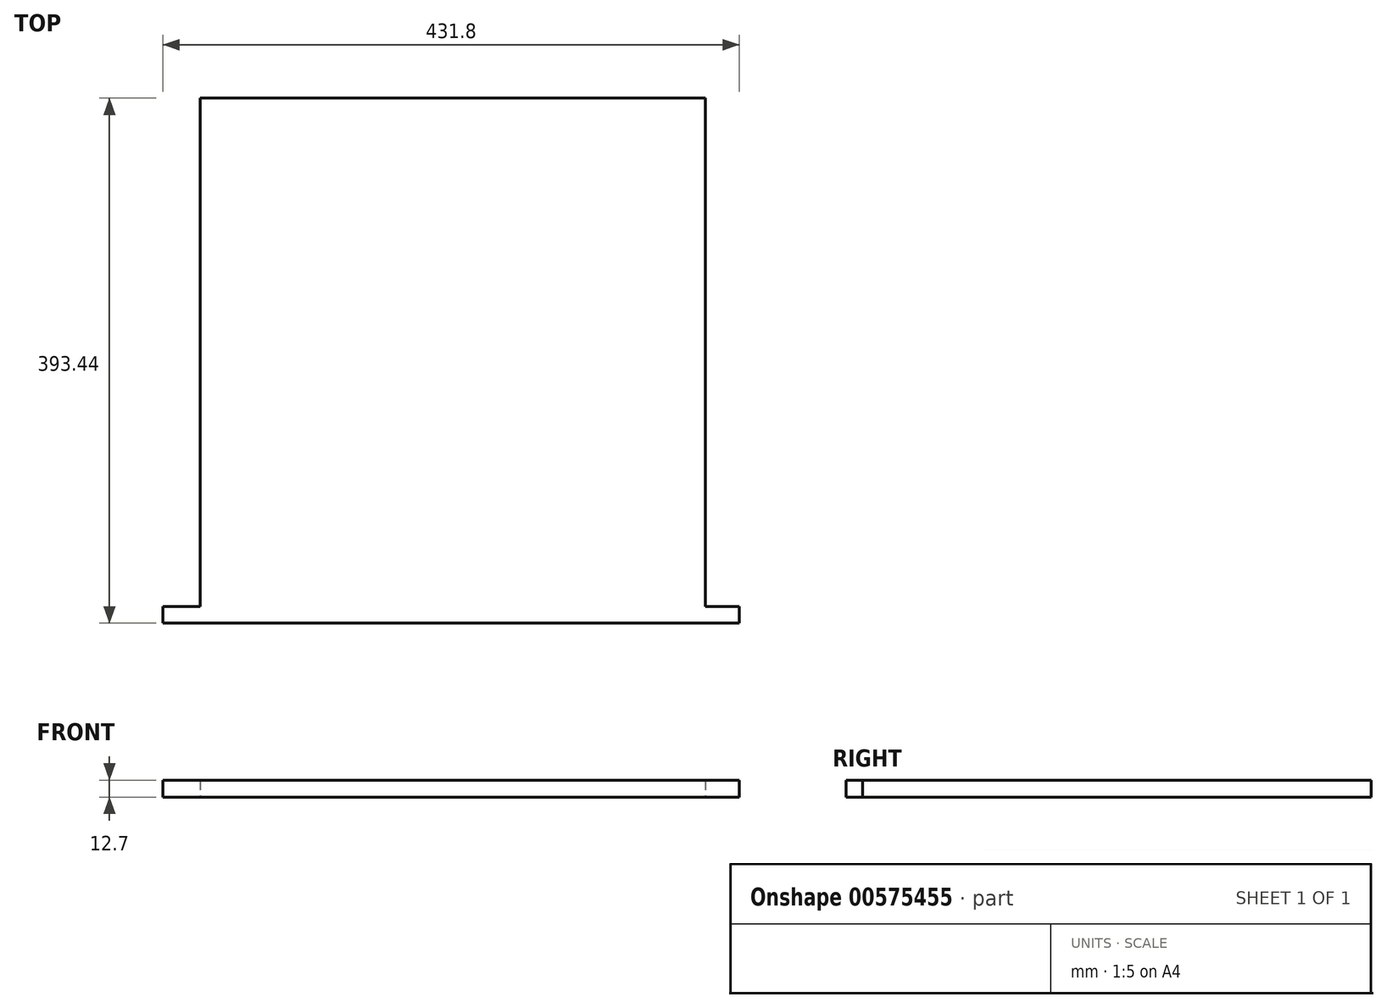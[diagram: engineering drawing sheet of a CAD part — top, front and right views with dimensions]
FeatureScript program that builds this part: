
annotation { "Feature Type Name" : "Feature", "Feature Type Description" : "" }
export const myFeature = defineFeature(function(context is Context, id is Id, definition is map)
    precondition{}
    {
        {
            var Q0;
            Q0=qCreatedBy(makeId("Top.planeOp"),FACE);
            var sketch = newSketch(context, id + "F0", { "sketchPlane" : qUnion([Q0])});
            skLineSegment(sketch, "E0", {"start": v(-215.51, -21.57) * mm, "end": v(-215.51, -34.01) * mm});
            skLineSegment(sketch, "E1", {"start": v(-215.51, -34.01) * mm, "end": v(216.29, -34.01) * mm});
            skLineSegment(sketch, "E2", {"start": v(216.29, -34.01) * mm, "end": v(216.29, -21.57) * mm});
            skLineSegment(sketch, "E3", {"start": v(-215.51, -21.57) * mm, "end": v(-187.57, -21.57) * mm});
            skLineSegment(sketch, "E4", {"start": v(-187.57, -21.57) * mm, "end": v(-187.57, 359.43) * mm});
            skLineSegment(sketch, "E5", {"start": v(216.29, -21.57) * mm, "end": v(190.89, -21.57) * mm});
            skLineSegment(sketch, "E6", {"start": v(190.89, -21.57) * mm, "end": v(190.89, 359.43) * mm});
            skLineSegment(sketch, "E7", {"start": v(190.89, 359.43) * mm, "end": v(-187.57, 359.43) * mm});
            skSolve(sketch);
        }
        {
            var Q0;
            Q0 = qSketchRegion(id + "F0", true);
            extrude(context, id + "F1", {"entities" : qUnion([Q0]), "depth" : 12.7 * mm, "offsetDistance" : 25.4 * mm});
        }
    });
